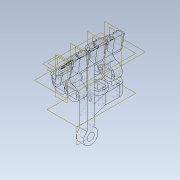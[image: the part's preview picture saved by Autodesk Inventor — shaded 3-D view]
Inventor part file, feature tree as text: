
AUTODESK INVENTOR PART (.ipt)
format: ipt  version: 2020.2 (Build 242310000, 310)  size: 1,063,424 bytes
history: native  units: mm
features: extrude x31, sketch x30, plane x10, other x4, fillet x1
ambient origin geometry x8: Origin, YZ Plane, XZ Plane, XY Plane, X Axis, Y Axis, Z Axis, Center Point
bodies: Solid1 (feature_tree)
feature tree (76):
  sketch  "Sketch1"  dims[d0=24.0mm d1=24.0mm]
  plane  "Work Plane1"
  plane  "Work Plane3"
  plane  "Work Plane4"
  sketch  "Sketch2"  dims[d2=24.0mm d4=5.0mm]
  extrude  "pinky_joint"  Depth=24.0mm
  other  "plane_pinky"
  plane  "Work Plane6"
  extrude  "finger_union"  Depth=5.0mm
  plane  "Work Plane16"
  extrude  "pinky_actuator_hole"  Depth=5.0mm
  other  "plane_ring"
  extrude  "ring_base"  Depth=10.0mm
  other  "plane_middle"
  other  "plane_index"
  extrude  "middle_base"  Depth=15.0mm
  extrude  "index_base"  Depth=10.0mm TaperAngle=0.0deg
  sketch  "Sketch46"  dims[d113=10.0mm d114=8.0mm d115=0.0mm]
  sketch  "Sketch51"  dims[d124=3.0mm d125=10.0mm]
  extrude  "ring_motor"  Depth=5.0mm
  extrude  "middle_motor"  Depth=10.0mm TaperAngle=0.0deg
  extrude  "index_motor"  Depth=10.0mm
  extrude  "pinky_motor"  Depth=3.0mm
  extrude  "Extrusion48"  Depth=10.0mm TaperAngle=0.0deg
  extrude  "Extrusion50"  Depth=5.0mm
  extrude  "Extrusion46"  Depth=14.0mm TaperAngle=0.0deg
  extrude  "Extrusion52"  Depth=5.0mm TaperAngle=0.0deg
  extrude  "Extrusion54"  Depth=14.0mm TaperAngle=0.0deg
  extrude  "Extrusion55"  [1 undecoded]
  plane  "Work Plane12"
  extrude  "spine_hand"  Depth=4.5mm
  plane  "Work Plane13"
  extrude  "thumb_motor_"  Depth=14.987mm TaperAngle=0.0deg
  extrude  "Extrusion56"  Depth=10.0mm
  plane  "Work Plane15"
  extrude  "Extrusion57"  Depth=6.0mm
  extrude  "Extrusion43"  Depth=60.0mm TaperAngle=360.0deg
  extrude  "Extrusion44"  Depth=4.5mm
  extrude  "Extrusion45"  Depth=15.0mm
  extrude  "Extrusion58"  Depth=6.0mm
  extrude  "Extrusion59"  Depth=5.0mm
  extrude  "Extrusion60"  Depth=10.0mm
  extrude  "pinky_holder"  Depth=5.0mm TaperAngle=0.0deg
  extrude  "ring_holder"  Depth=5.0mm
  extrude  "middle_holder"  Depth=10.0mm
  extrude  "index_holder"  Depth=5.0mm TaperAngle=0.0deg
  fillet  "Fillet6"  Radius=15.0mm
  plane  "Work Plane17"
  extrude  "Extrusion65"  Depth=5.0mm
  plane  "Work Plane2"
  sketch  "Sketch23"  dims[d5=8.0mm d6=5.0mm]
  sketch  "Sketch24"  dims[d7=3.0mm d8=10.0mm]
  sketch  "Sketch25"  dims[d15=8.0mm d16=0.0mm d80=15.0mm]
  sketch  "Sketch27"  dims[d81=10.0mm d106=72.0mm d107=0.0mm]
  sketch  "Sketch28"  dims[d110=5.0mm d111=0.0mm d112=3.0mm]
  sketch  "Sketch52"  dims[d126=8.0mm d127=0.0mm d128=3.0mm]
  sketch  "Sketch53"  dims[d129=10.0mm d130=8.0mm d131=0.0mm]
  sketch  "Sketch58"  dims[d227=15.0mm d230=20.0mm d235=5.0mm d237=9.0mm]
  sketch  "Sketch62"  dims[d238=14.0mm d239=2.0mm d240=0.0mm d241=0.0mm d242=14.0mm d243=2.0mm d244=0.0mm d245=0.0mm]
  sketch  "Sketch63"  dims[d254=5.0mm d257=14.0mm d258=2.0mm d259=0.0mm d260=0.0mm]
  sketch  "Sketch64"  dims[d273=20.0mm d278=14.0mm d279=2.0mm d280=0.0mm d281=0.0mm]
  sketch  "Sketch65"  dims[d310=80.0mm d311=0.0mm d312=-48.0mm]
  sketch  "Sketch67"  dims[d320=14.0mm d321=0.0mm d349=4.5mm]
  sketch  "Sketch69"  dims[d350=3.0mm d351=14.987mm d352=0.0mm]
  sketch  "Sketch71"  dims[d353=10.0mm d354=3.0mm]
  sketch  "Sketch73"  dims[d355=35.5mm d356=0.0mm d357=6.0mm]
  sketch  "Sketch75"  dims[d358=120.0deg d359=60.0mm d361=360.0deg]
  sketch  "Sketch76"  dims[d363=2.0mm d364=0.0mm d367=4.5mm]
  sketch  "Sketch77"  dims[d368=0.0mm d369=15.0mm]
  sketch  "Sketch78"  dims[d370=9.0mm d371=6.0mm]
  sketch  "Sketch79"  dims[d372=5.0mm d373=12.0mm]
  sketch  "Sketch80"  dims[d374=10.0mm d375=0.2mm]
  sketch  "Sketch81"  dims[d376=5.0mm d377=3.0mm d378=0.0mm]
  sketch  "Sketch82"  dims[d382=6.0mm d383=5.0mm]
  sketch  "Sketch83"  dims[d384=12.0mm d385=10.0mm]
  sketch  "Sketch84"  dims[d386=0.2mm d387=3.0mm d388=0.0mm d392=15.0mm d393=9.0mm d394=6.0mm d395=5.0mm d396=12.0mm d397=10.0mm d398=0.2mm d399=5.0mm d400=3.0mm d401=0.0mm d405=15.0mm d406=9.0mm d407=5.0mm d408=3.0mm d409=0.0mm d412=3.0mm d413=3.0mm d414=55.0mm d415=0.0mm d416=3.0mm d417=52.0mm d418=0.0mm d428=1.9mm d429=3.0mm d430=1.9mm d431=3.0mm d432=76.0mm d433=0.0mm d435=14.0mm d436=10.0mm d437=10.0mm d438=5.0mm d439=5.0mm d440=0.0mm d442=20.0mm d443=20.0mm d444=5.2mm d445=6.2mm d446=5.2mm d447=6.2mm d448=12.4mm d449=10.4mm d450=12.4mm d451=10.4mm d452=25.0mm d453=10.0mm d454=5.0mm d455=10.0mm d456=20.0mm d457=10.0mm d458=0.0mm d459=15.0mm d460=10.0mm d461=0.0mm d462=10.0mm d463=0.0mm d464=17.0mm d465=20.0mm d466=0.0mm d467=17.0mm d468=20.0mm d469=0.0mm d470=17.0mm d471=20.0mm d472=0.0mm d473=17.0mm d474=20.0mm d475=0.0mm d476=135.0deg d477=7.5mm d478=5.0mm d479=1.5mm d480=1.5mm d481=4.0mm d482=7.5mm d483=5.0mm d484=45.0deg d485=1.5mm d486=1.5mm d487=7.5mm d488=5.0mm d489=1.5mm d490=1.5mm d491=45.0deg d492=7.5mm d493=5.0mm d494=1.5mm d495=1.5mm d496=45.0deg d497=2.0mm d498=2.0mm d499=2.0mm d500=2.0mm d501=2.0mm d502=2.0mm d503=2.0mm d504=2.0mm d505=28.0mm d506=0.0mm d507=3.0mm d77=0.5mm d78=0.872665mm d79=0.5mm d341=0.5mm d342=0.872665mm d343=0.5mm d344=0.872665mm]
note: 1 required parameter value undecoded (feature->parameter linkage not recoverable at this tier; creation-order binding heuristic only, values carry confidence <= 0.55)
